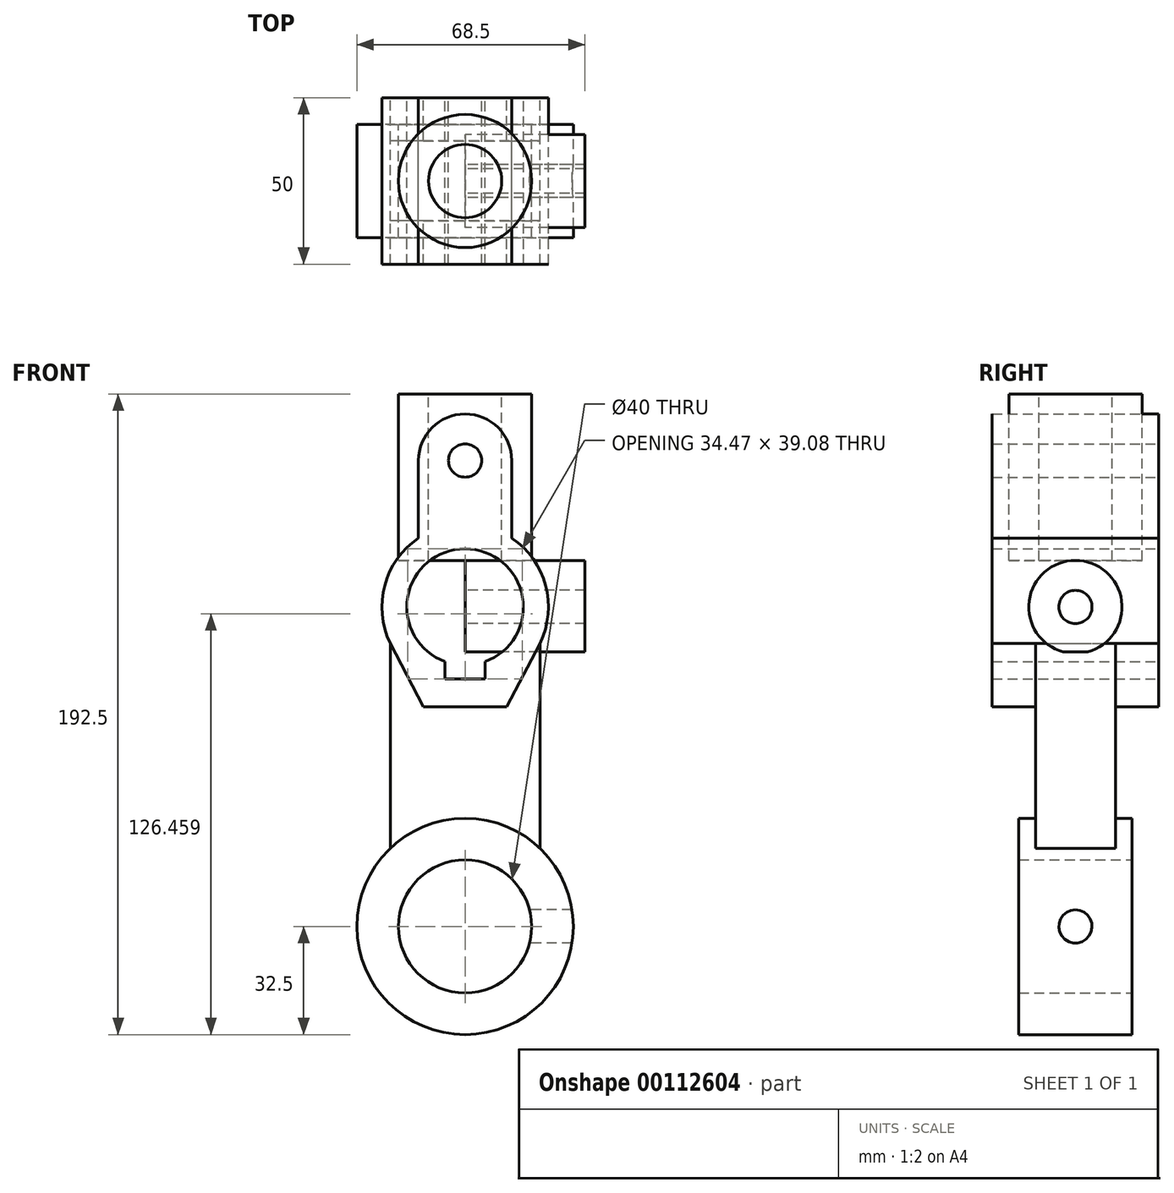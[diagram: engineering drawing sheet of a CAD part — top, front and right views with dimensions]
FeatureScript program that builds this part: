
annotation { "Feature Type Name" : "Feature", "Feature Type Description" : "" }
export const myFeature = defineFeature(function(context is Context, id is Id, definition is map)
    precondition{}
    {
        {
            var Q0;
            Q0=qCreatedBy(makeId("Front.planeOp"),FACE);
            var sketch = newSketch(context, id + "F0", { "sketchPlane" : qUnion([Q0])});
            skCircle(sketch, "E0", {"center": v(0, 0) * mm, "radius": 20 * mm});
            skCircle(sketch, "E1", {"center": v(0, 0) * mm, "radius": 32.5 * mm});
            skLineSegment(sketch, "E2", {"start": v(0, 0) * mm, "end": v(0, 192) * mm, "construction": true});
            skArc(sketch, "E3", {"start": v(6, 79.56) * mm, "mid": v(0, 113.5) * mm, "end": v(-6, 79.56) * mm});
            skCircle(sketch, "E4", {"center": v(0, 140) * mm, "radius": 5 * mm});
            skArc(sketch, "E5", {"start": v(-14, 140) * mm, "mid": v(0, 154) * mm, "end": v(14, 140) * mm});
            skLineSegment(sketch, "E6", {"start": v(-6, 79.56) * mm, "end": v(-6, 74.42) * mm});
            skLineSegment(sketch, "E7.MirrorCS", {"start": v(6, 79.56) * mm, "end": v(6, 74.42) * mm});
            skLineSegment(sketch, "E8", {"start": v(-6, 74.42) * mm, "end": v(6, 74.42) * mm});
            skArc(sketch, "E9", {"start": v(-14, 116.71) * mm, "mid": v(-24.14, 102.5) * mm, "end": v(-22.5, 85.1) * mm});
            skLineSegment(sketch, "E10", {"start": v(0, 66) * mm, "end": v(-12.5, 66) * mm});
            skLineSegment(sketch, "E11.MirrorCS", {"start": v(0, 66) * mm, "end": v(12.5, 66) * mm});
            skLineSegment(sketch, "E12", {"start": v(-12.5, 66) * mm, "end": v(-22.5, 85.1) * mm});
            skLineSegment(sketch, "E13", {"start": v(12.5, 66) * mm, "end": v(22.5, 85.1) * mm});
            skLineSegment(sketch, "E14", {"start": v(-14, 140) * mm, "end": v(-14, 116.71) * mm});
            skLineSegment(sketch, "E15", {"start": v(14, 140) * mm, "end": v(14, 116.71) * mm});
            skArc(sketch, "E16.trimOffspring", {"start": v(22.5, 85.1) * mm, "mid": v(24.14, 102.5) * mm, "end": v(14, 116.71) * mm});
            skLineSegment(sketch, "E17", {"start": v(-22.5, 85.1) * mm, "end": v(-22.5, 23.45) * mm});
            skLineSegment(sketch, "E18.MirrorCS", {"start": v(22.5, 85.1) * mm, "end": v(22.5, 23.45) * mm});
            skSolve(sketch);
        }
        {
            var Q0;
            Q0=qCreatedBy(makeId("Right.planeOp"),FACE);
            var sketch = newSketch(context, id + "F1", { "sketchPlane" : qUnion([Q0])});
            skCircle(sketch, "E19", {"center": v(0, 96) * mm, "radius": 14 * mm});
            skCircle(sketch, "E20", {"center": v(0, 96) * mm, "radius": 5 * mm});
            skCircle(sketch, "E21", {"center": v(0, 0) * mm, "radius": 5 * mm});
            skLineSegment(sketch, "E22.bottom", {"start": v(-12, 82.48) * mm, "end": v(12, 82.48) * mm});
            skLineSegment(sketch, "E22.top", {"start": v(-12, 23.45) * mm, "end": v(12, 23.45) * mm});
            skLineSegment(sketch, "E22.left", {"start": v(-12, 82.48) * mm, "end": v(-12, 23.45) * mm});
            skLineSegment(sketch, "E22.right", {"start": v(12, 82.48) * mm, "end": v(12, 23.45) * mm});
            skSolve(sketch);
        }
        {
            var Q0;
            Q0=qCreatedBy(makeId("Right.planeOp"),FACE);
            var sketch = newSketch(context, id + "F2", { "sketchPlane" : qUnion([Q0])});
            skSolve(sketch);
        }
        {
            var Q0;
            Q0=qCreatedBy(makeId("Top.planeOp"),FACE);
            cPlane(context, id + "F3", {"entities" : qUnion([Q0]), "cplaneType" : CPlaneType.OFFSET, "offset" : 160 * mm, "width" : 150 * mm, "height" : 150 * mm});
        }
        {
            var Q0;
            Q0=qCreatedBy(id+"F3.planeOp",FACE);
            var sketch = newSketch(context, id + "F4", { "sketchPlane" : qUnion([Q0])});
            skCircle(sketch, "E23", {"center": v(0, 0) * mm, "radius": 11 * mm});
            skCircle(sketch, "E24", {"center": v(0, 0) * mm, "radius": 20 * mm});
            skSolve(sketch);
        }
        {
            var Q0;
            Q0=qSketchRegion(id+"F4",true);
            extrude(context, id + "F5", {"entities" : qUnion([Q0]), "oppositeDirection" : true, "depth" : 50 * mm});
        }
        {
            var Q0;
            Q0=makeQuery(id+"F0.imprint","IMPRINT",FACE,{"disambiguationData":[TD([[makeQuery(id+"F0.imprint","IMPRINT",EDGE,{"derivedFrom":sQuery(id+"F0.wireOp",EDGE,"E3")}),-1.0]])]});
            extrude(context, id + "F6", {"entities" : qUnion([Q0]), "endBound" : BoundingType.SYMMETRIC, "depth" : 50 * mm});
        }
        {
            var Q0;
            Q0=makeQuery(id+"F0.imprint","IMPRINT",FACE,{"disambiguationData":[TD([[makeQuery(id+"F0.imprint","IMPRINT",EDGE,{"derivedFrom":sQuery(id+"F0.wireOp",EDGE,"E0")}),-1.0]])]});
            var Q1;
            Q1=qSketchRegion(id+"F2",true);
            extrude(context, id + "F7", {"entities" : qUnion([Q0, Q1]), "endBound" : BoundingType.SYMMETRIC, "depth" : 34 * mm});
        }
        {
            var Q0;
            Q0=makeQuery(id+"F1.imprint","IMPRINT",FACE,{"disambiguationData":[TD([[makeQuery(id+"F1.imprint","IMPRINT",EDGE,{"derivedFrom":sQuery(id+"F1.wireOp",EDGE,"E21")}),1.0]])]});
            var Q1;
            Q1=sQuery(id+"F1.wireOp",EDGE,"E21");
            extrude(context, id + "F8", {"entities" : qUnion([Q0]), "operationType" : NewBodyOperationType.REMOVE, "surfaceEntities" : qUnion([Q1]), "depth" : 100 * mm});
        }
        {
            var Q0;
            Q0=makeQuery(id+"F0.imprint","IMPRINT",FACE,{"disambiguationData":[TD([[makeQuery(id+"F0.imprint","IMPRINT",EDGE,{"derivedFrom":sQuery(id+"F0.wireOp",EDGE,"E10")}),1.0]])]});
            extrude(context, id + "F9", {"entities" : qUnion([Q0]), "operationType" : NewBodyOperationType.ADD, "endBound" : BoundingType.SYMMETRIC, "depth" : 24 * mm});
        }
        {
            var Q0;
            Q0=makeQuery(id+"F1.imprint","IMPRINT",FACE,{"disambiguationData":[TD([[makeQuery(id+"F1.imprint","IMPRINT",EDGE,{"derivedFrom":sQuery(id+"F1.wireOp",EDGE,"E20")}),-1.0]])]});
            var Q1;
            Q1=sQuery(id+"F1.wireOp",EDGE,"E19");
            var Q2;
            Q2=sQuery(id+"F1.wireOp",EDGE,"E20");
            extrude(context, id + "F10", {"entities" : qUnion([Q0]), "surfaceEntities" : qUnion([Q1, Q2]), "depth" : 36 * mm});
        }
    });
